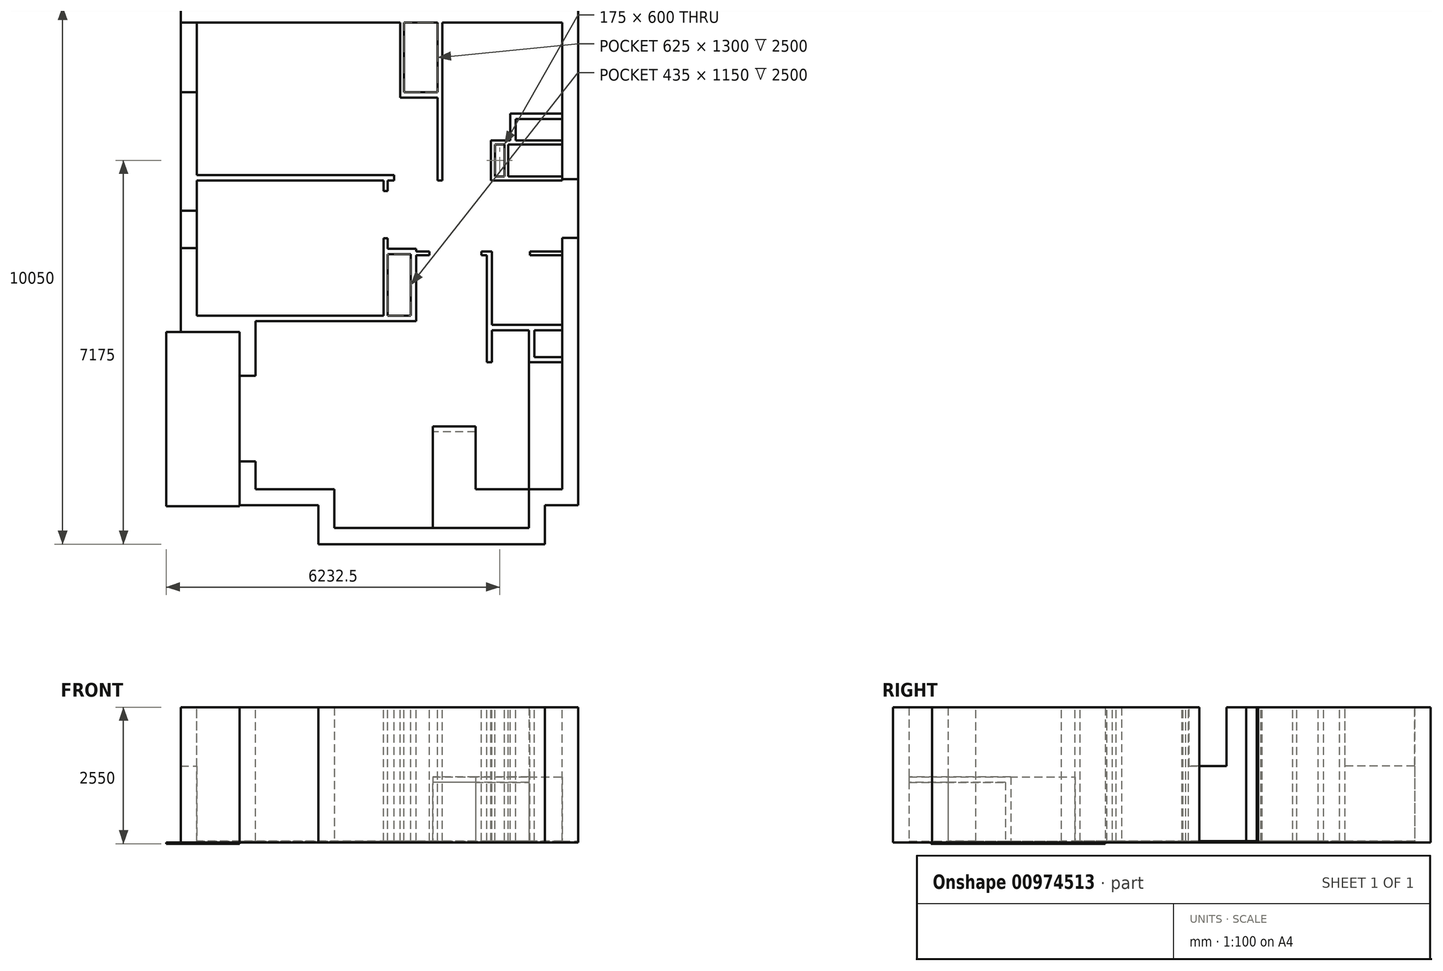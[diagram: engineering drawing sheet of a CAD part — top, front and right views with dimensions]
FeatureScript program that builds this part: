
annotation { "Feature Type Name" : "Feature", "Feature Type Description" : "" }
export const myFeature = defineFeature(function(context is Context, id is Id, definition is map)
    precondition{}
    {
        {
            var Q0;
            Q0=qCreatedBy(makeId("Top.planeOp"),FACE);
            var sketch = newSketch(context, id + "F0", { "sketchPlane" : qUnion([Q0])});
            skLineSegment(sketch, "E0", {"start": v(0, 0) * mm, "end": v(-6830, 0) * mm});
            skLineSegment(sketch, "E1", {"start": v(-6830, 0) * mm, "end": v(-6830, -5480) * mm});
            skLineSegment(sketch, "E2", {"start": v(-6830, -5480) * mm, "end": v(-5730, -5480) * mm});
            skLineSegment(sketch, "E3", {"start": v(-5730, -5480) * mm, "end": v(-5730, -8720) * mm});
            skLineSegment(sketch, "E4", {"start": v(-5730, -8720) * mm, "end": v(-4260, -8720) * mm});
            skLineSegment(sketch, "E5", {"start": v(-4260, -8720) * mm, "end": v(-4260, -9450) * mm});
            skLineSegment(sketch, "E6", {"start": v(-4260, -9450) * mm, "end": v(-620, -9450) * mm});
            skLineSegment(sketch, "E7", {"start": v(-620, -9450) * mm, "end": v(-620, -8720) * mm});
            skLineSegment(sketch, "E8", {"start": v(-620, -8720) * mm, "end": v(0, -8720) * mm});
            skLineSegment(sketch, "E9", {"start": v(0, -8720) * mm, "end": v(0, 0) * mm});
            skLineSegment(sketch, "E10", {"start": v(-7130, 300) * mm, "end": v(300, 300) * mm});
            skLineSegment(sketch, "E11", {"start": v(300, 300) * mm, "end": v(300, -9020) * mm});
            skLineSegment(sketch, "E12", {"start": v(300, -9020) * mm, "end": v(-320, -9020) * mm});
            skLineSegment(sketch, "E13", {"start": v(-320, -9020) * mm, "end": v(-320, -9750) * mm});
            skLineSegment(sketch, "E14", {"start": v(-320, -9750) * mm, "end": v(-4560, -9750) * mm});
            skLineSegment(sketch, "E15", {"start": v(-4560, -9750) * mm, "end": v(-4560, -9020) * mm});
            skLineSegment(sketch, "E16", {"start": v(-4560, -9020) * mm, "end": v(-6030, -9020) * mm});
            skLineSegment(sketch, "E17", {"start": v(-6030, -9020) * mm, "end": v(-6030, -5780) * mm});
            skLineSegment(sketch, "E18", {"start": v(-6030, -5780) * mm, "end": v(-7130, -5780) * mm});
            skLineSegment(sketch, "E19", {"start": v(-7130, -5780) * mm, "end": v(-7130, 300) * mm});
            skSolve(sketch);
        }
        {
            var Q0;
            Q0 = qSketchRegion(id + "F0", true);
            extrude(context, id + "F1", {"entities" : qUnion([Q0]), "depth" : 2500 * mm, "offsetDistance" : 25 * mm});
        }
        {
            var Q0;
            Q0=makeQuery(id+"F1.opExtrude","CAP_FACE",FACE,{"disambiguationData":[OSD([sQuery(id+"F0.wireOp",EDGE,"E0"),sQuery(id+"F0.wireOp",EDGE,"E1"),sQuery(id+"F0.wireOp",EDGE,"E2"),sQuery(id+"F0.wireOp",EDGE,"E3"),sQuery(id+"F0.wireOp",EDGE,"E4"),sQuery(id+"F0.wireOp",EDGE,"E5"),sQuery(id+"F0.wireOp",EDGE,"E6"),sQuery(id+"F0.wireOp",EDGE,"E7"),sQuery(id+"F0.wireOp",EDGE,"E8"),sQuery(id+"F0.wireOp",EDGE,"E9"),sQuery(id+"F0.wireOp",EDGE,"E10"),sQuery(id+"F0.wireOp",EDGE,"E11"),sQuery(id+"F0.wireOp",EDGE,"E12"),sQuery(id+"F0.wireOp",EDGE,"E13"),sQuery(id+"F0.wireOp",EDGE,"E14"),sQuery(id+"F0.wireOp",EDGE,"E15"),sQuery(id+"F0.wireOp",EDGE,"E16"),sQuery(id+"F0.wireOp",EDGE,"E17"),sQuery(id+"F0.wireOp",EDGE,"E18"),sQuery(id+"F0.wireOp",EDGE,"E19")])],"isStart":true});
            var sketch = newSketch(context, id + "F2", { "sketchPlane" : qUnion([Q0])});
            skLineSegment(sketch, "E20.0", {"start": v(-7130, -300) * mm, "end": v(300, -300) * mm});
            skLineSegment(sketch, "E20.1", {"start": v(-7130, 5780) * mm, "end": v(-7130, -300) * mm});
            skLineSegment(sketch, "E20.2", {"start": v(-6030, 5780) * mm, "end": v(-7130, 5780) * mm});
            skLineSegment(sketch, "E20.3", {"start": v(-6030, 9020) * mm, "end": v(-6030, 5780) * mm});
            skLineSegment(sketch, "E20.4", {"start": v(-4560, 9020) * mm, "end": v(-6030, 9020) * mm});
            skLineSegment(sketch, "E20.5", {"start": v(-4560, 9750) * mm, "end": v(-4560, 9020) * mm});
            skLineSegment(sketch, "E20.6", {"start": v(-320, 9750) * mm, "end": v(-4560, 9750) * mm});
            skLineSegment(sketch, "E20.7", {"start": v(-320, 9020) * mm, "end": v(-320, 9750) * mm});
            skLineSegment(sketch, "E20.8", {"start": v(300, 9020) * mm, "end": v(-320, 9020) * mm});
            skLineSegment(sketch, "E20.9", {"start": v(300, -300) * mm, "end": v(300, 9020) * mm});
            skSolve(sketch);
        }
        {
            var Q0;
            Q0 = qSketchRegion(id + "F2", true);
            extrude(context, id + "F3", {"entities" : qUnion([Q0]), "operationType" : NewBodyOperationType.ADD, "depth" : 25 * mm, "offsetDistance" : 25 * mm});
        }
        {
            var Q0;
            Q0=makeQuery(id+"F3.opExtrude","CAP_FACE",FACE,{"disambiguationData":[OSD([sQuery(id+"F2.wireOp",EDGE,"E20.0"),sQuery(id+"F2.wireOp",EDGE,"E20.1"),sQuery(id+"F2.wireOp",EDGE,"E20.2"),sQuery(id+"F2.wireOp",EDGE,"E20.3"),sQuery(id+"F2.wireOp",EDGE,"E20.4"),sQuery(id+"F2.wireOp",EDGE,"E20.5"),sQuery(id+"F2.wireOp",EDGE,"E20.6"),sQuery(id+"F2.wireOp",EDGE,"E20.7"),sQuery(id+"F2.wireOp",EDGE,"E20.8"),sQuery(id+"F2.wireOp",EDGE,"E20.9")])],"isStart":false});
            var sketch = newSketch(context, id + "F4", { "sketchPlane" : qUnion([Q0])});
            skLineSegment(sketch, "E21", {"start": v(-6030, 5780) * mm, "end": v(-7400, 5780) * mm});
            skLineSegment(sketch, "E22", {"start": v(-7400, 5780) * mm, "end": v(-7400, 9040) * mm});
            skLineSegment(sketch, "E23", {"start": v(-7400, 9040) * mm, "end": v(-6030, 9040) * mm});
            skLineSegment(sketch, "E24", {"start": v(-6030, 9040) * mm, "end": v(-6030, 5780) * mm});
            skSolve(sketch);
        }
        {
            var Q0;
            Q0 = qSketchRegion(id + "F4", true);
            extrude(context, id + "F5", {"entities" : qUnion([Q0]), "depth" : 25 * mm, "offsetDistance" : 25 * mm});
        }
        {
            var Q0;
            Q0=makeQuery(id+"F1.opExtrude","CAP_FACE",FACE,{"disambiguationData":[OSD([sQuery(id+"F0.wireOp",EDGE,"E0"),sQuery(id+"F0.wireOp",EDGE,"E1"),sQuery(id+"F0.wireOp",EDGE,"E2"),sQuery(id+"F0.wireOp",EDGE,"E3"),sQuery(id+"F0.wireOp",EDGE,"E4"),sQuery(id+"F0.wireOp",EDGE,"E5"),sQuery(id+"F0.wireOp",EDGE,"E6"),sQuery(id+"F0.wireOp",EDGE,"E7"),sQuery(id+"F0.wireOp",EDGE,"E8"),sQuery(id+"F0.wireOp",EDGE,"E9"),sQuery(id+"F0.wireOp",EDGE,"E10"),sQuery(id+"F0.wireOp",EDGE,"E11"),sQuery(id+"F0.wireOp",EDGE,"E12"),sQuery(id+"F0.wireOp",EDGE,"E13"),sQuery(id+"F0.wireOp",EDGE,"E14"),sQuery(id+"F0.wireOp",EDGE,"E15"),sQuery(id+"F0.wireOp",EDGE,"E16"),sQuery(id+"F0.wireOp",EDGE,"E17"),sQuery(id+"F0.wireOp",EDGE,"E18"),sQuery(id+"F0.wireOp",EDGE,"E19")])],"isStart":false});
            var sketch = newSketch(context, id + "F6", { "sketchPlane" : qUnion([Q0])});
            skLineSegment(sketch, "E25", {"start": v(-6830, -2950) * mm, "end": v(-3340, -2950) * mm});
            skLineSegment(sketch, "E26", {"start": v(-5730, -5480) * mm, "end": v(-3340, -5480) * mm});
            skLineSegment(sketch, "E27", {"start": v(-5730, -5580) * mm, "end": v(-2730, -5580) * mm});
            skLineSegment(sketch, "E28", {"start": v(-2730, -5580) * mm, "end": v(-2730, -4350) * mm});
            skLineSegment(sketch, "E29", {"start": v(-2730, -4230) * mm, "end": v(-3265, -4230) * mm});
            skLineSegment(sketch, "E30", {"start": v(-2830, -5480) * mm, "end": v(-2830, -4330) * mm});
            skLineSegment(sketch, "E31", {"start": v(-2830, -4330) * mm, "end": v(-3265, -4330) * mm});
            skLineSegment(sketch, "E32", {"start": v(-3265, -4330) * mm, "end": v(-3265, -5480) * mm});
            skLineSegment(sketch, "E33", {"start": v(-3340, -4230) * mm, "end": v(-3340, -5480) * mm});
            skLineSegment(sketch, "E34", {"start": v(-2330, 0) * mm, "end": v(-2330, -1300) * mm});
            skLineSegment(sketch, "E35", {"start": v(-2330, -2950) * mm, "end": v(-2240, -2950) * mm});
            skLineSegment(sketch, "E36", {"start": v(-2240, -2950) * mm, "end": v(-2240, 0) * mm});
            skLineSegment(sketch, "E37", {"start": v(-5730, -5580) * mm, "end": v(-5730, -5480) * mm});
            skLineSegment(sketch, "E38", {"start": v(-2240, 0) * mm, "end": v(-2330, 0) * mm});
            skLineSegment(sketch, "E39.trimOffspring", {"start": v(-3265, -5480) * mm, "end": v(-2830, -5480) * mm});
            skLineSegment(sketch, "E40", {"start": v(-3265, -4230) * mm, "end": v(-3265, -4030) * mm});
            skLineSegment(sketch, "E41", {"start": v(-3265, -4030) * mm, "end": v(-3340, -4030) * mm});
            skLineSegment(sketch, "E42", {"start": v(-3340, -4030) * mm, "end": v(-3340, -4230) * mm});
            skLineSegment(sketch, "E43", {"start": v(-2955, 0) * mm, "end": v(-2955, -1300) * mm});
            skLineSegment(sketch, "E44", {"start": v(-2955, -1300) * mm, "end": v(-2330, -1300) * mm});
            skLineSegment(sketch, "E45", {"start": v(-2330, -1400) * mm, "end": v(-3030, -1400) * mm});
            skLineSegment(sketch, "E46", {"start": v(-3030, -1400) * mm, "end": v(-3030, 0) * mm});
            skLineSegment(sketch, "E47", {"start": v(-3030, 0) * mm, "end": v(-2955, 0) * mm});
            skLineSegment(sketch, "E48.trimOffspring", {"start": v(-2330, -1400) * mm, "end": v(-2330, -2950) * mm});
            skLineSegment(sketch, "E49", {"start": v(-3265, -2950) * mm, "end": v(-3265, -3150) * mm});
            skLineSegment(sketch, "E50", {"start": v(-3265, -3150) * mm, "end": v(-3340, -3150) * mm});
            skLineSegment(sketch, "E51", {"start": v(-3340, -3150) * mm, "end": v(-3340, -2950) * mm});
            skLineSegment(sketch, "E52", {"start": v(-3140, -2850) * mm, "end": v(-3140, -2950) * mm});
            skLineSegment(sketch, "E53", {"start": v(-3140, -2950) * mm, "end": v(-3265, -2950) * mm});
            skLineSegment(sketch, "E54", {"start": v(-6830, -2850) * mm, "end": v(-3140, -2850) * mm});
            skLineSegment(sketch, "E55", {"start": v(-6830, -2950) * mm, "end": v(-6830, -2850) * mm});
            skLineSegment(sketch, "E56", {"start": v(-2730, -4275) * mm, "end": v(-2480, -4275) * mm});
            skLineSegment(sketch, "E57", {"start": v(-2480, -4275) * mm, "end": v(-2480, -4350) * mm});
            skLineSegment(sketch, "E58", {"start": v(-2480, -4350) * mm, "end": v(-2730, -4350) * mm});
            skLineSegment(sketch, "E59.trimOffspring", {"start": v(-2730, -4275) * mm, "end": v(-2730, -4230) * mm});
            skSolve(sketch);
        }
        {
            var Q0;
            Q0 = qSketchRegion(id + "F6", true);
            extrude(context, id + "F7", {"entities" : qUnion([Q0]), "operationType" : NewBodyOperationType.ADD, "endBound" : BoundingType.UP_TO_NEXT, "oppositeDirection" : true, "depth" : 25 * mm, "offsetDistance" : 25 * mm});
        }
        {
            var Q0;
            Q0=makeQuery(id+"F7.boolean.opBoolean","MERGE",FACE,{"derivedFrom":[makeQuery(id+"F1.opExtrude","CAP_FACE",FACE,{"disambiguationData":[OSD([sQuery(id+"F0.wireOp",EDGE,"E0"),sQuery(id+"F0.wireOp",EDGE,"E1"),sQuery(id+"F0.wireOp",EDGE,"E2"),sQuery(id+"F0.wireOp",EDGE,"E3"),sQuery(id+"F0.wireOp",EDGE,"E4"),sQuery(id+"F0.wireOp",EDGE,"E5"),sQuery(id+"F0.wireOp",EDGE,"E6"),sQuery(id+"F0.wireOp",EDGE,"E7"),sQuery(id+"F0.wireOp",EDGE,"E8"),sQuery(id+"F0.wireOp",EDGE,"E9"),sQuery(id+"F0.wireOp",EDGE,"E10"),sQuery(id+"F0.wireOp",EDGE,"E11"),sQuery(id+"F0.wireOp",EDGE,"E12"),sQuery(id+"F0.wireOp",EDGE,"E13"),sQuery(id+"F0.wireOp",EDGE,"E14"),sQuery(id+"F0.wireOp",EDGE,"E15"),sQuery(id+"F0.wireOp",EDGE,"E16"),sQuery(id+"F0.wireOp",EDGE,"E17"),sQuery(id+"F0.wireOp",EDGE,"E18"),sQuery(id+"F0.wireOp",EDGE,"E19")])],"isStart":false}),makeQuery(id+"F7.opExtrude","CAP_FACE",FACE,{"disambiguationData":[OSD([sQuery(id+"F6.wireOp",EDGE,"E25"),sQuery(id+"F6.wireOp",EDGE,"E49"),sQuery(id+"F6.wireOp",EDGE,"E50"),sQuery(id+"F6.wireOp",EDGE,"E51"),sQuery(id+"F6.wireOp",EDGE,"E52"),sQuery(id+"F6.wireOp",EDGE,"E53"),sQuery(id+"F6.wireOp",EDGE,"E54"),sQuery(id+"F6.wireOp",EDGE,"E55")])],"isStart":true}),makeQuery(id+"F7.opExtrude","CAP_FACE",FACE,{"disambiguationData":[OSD([sQuery(id+"F6.wireOp",EDGE,"E26"),sQuery(id+"F6.wireOp",EDGE,"E27"),sQuery(id+"F6.wireOp",EDGE,"E28"),sQuery(id+"F6.wireOp",EDGE,"E29"),sQuery(id+"F6.wireOp",EDGE,"E30"),sQuery(id+"F6.wireOp",EDGE,"E31"),sQuery(id+"F6.wireOp",EDGE,"E32"),sQuery(id+"F6.wireOp",EDGE,"E33"),sQuery(id+"F6.wireOp",EDGE,"E37"),sQuery(id+"F6.wireOp",EDGE,"E39.trimOffspring"),sQuery(id+"F6.wireOp",EDGE,"E40"),sQuery(id+"F6.wireOp",EDGE,"E41"),sQuery(id+"F6.wireOp",EDGE,"E42")])],"isStart":true}),makeQuery(id+"F7.opExtrude","CAP_FACE",FACE,{"disambiguationData":[OSD([sQuery(id+"F6.wireOp",EDGE,"E34"),sQuery(id+"F6.wireOp",EDGE,"E35"),sQuery(id+"F6.wireOp",EDGE,"E36"),sQuery(id+"F6.wireOp",EDGE,"E38"),sQuery(id+"F6.wireOp",EDGE,"E43"),sQuery(id+"F6.wireOp",EDGE,"E44"),sQuery(id+"F6.wireOp",EDGE,"E45"),sQuery(id+"F6.wireOp",EDGE,"E46"),sQuery(id+"F6.wireOp",EDGE,"E47"),sQuery(id+"F6.wireOp",EDGE,"E48.trimOffspring")])],"isStart":true})]});
            var sketch = newSketch(context, id + "F8", { "sketchPlane" : qUnion([Q0])});
            skLineSegment(sketch, "E60", {"start": v(0, -6350) * mm, "end": v(-620, -6350) * mm});
            skLineSegment(sketch, "E61", {"start": v(-620, -6350) * mm, "end": v(-620, -5750) * mm});
            skLineSegment(sketch, "E62", {"start": v(0, -5650) * mm, "end": v(0, -5750) * mm});
            skLineSegment(sketch, "E63", {"start": v(0, -5750) * mm, "end": v(-520, -5750) * mm});
            skLineSegment(sketch, "E64", {"start": v(-520, -5750) * mm, "end": v(-520, -6250) * mm});
            skLineSegment(sketch, "E65", {"start": v(-520, -6250) * mm, "end": v(0, -6250) * mm});
            skLineSegment(sketch, "E66", {"start": v(0, -6350) * mm, "end": v(0, -6250) * mm});
            skLineSegment(sketch, "E67", {"start": v(-620, -5750) * mm, "end": v(-1310, -5750) * mm});
            skLineSegment(sketch, "E68", {"start": v(-1310, -5750) * mm, "end": v(-1310, -6350) * mm});
            skLineSegment(sketch, "E69", {"start": v(-1310, -6350) * mm, "end": v(-1410, -6350) * mm});
            skLineSegment(sketch, "E70", {"start": v(-1410, -6350) * mm, "end": v(-1410, -4350) * mm});
            skLineSegment(sketch, "E71", {"start": v(-1410, -4350) * mm, "end": v(-1510, -4350) * mm});
            skLineSegment(sketch, "E72", {"start": v(-1510, -4350) * mm, "end": v(-1510, -4275) * mm});
            skLineSegment(sketch, "E73", {"start": v(-1510, -4275) * mm, "end": v(-1310, -4275) * mm});
            skLineSegment(sketch, "E74", {"start": v(-1310, -4275) * mm, "end": v(-1310, -5650) * mm});
            skLineSegment(sketch, "E75", {"start": v(-1310, -5650) * mm, "end": v(0, -5650) * mm});
            skLineSegment(sketch, "E76", {"start": v(0, -4350) * mm, "end": v(-600, -4350) * mm});
            skLineSegment(sketch, "E77", {"start": v(-600, -4350) * mm, "end": v(-600, -4275) * mm});
            skLineSegment(sketch, "E78", {"start": v(-600, -4275) * mm, "end": v(0, -4275) * mm});
            skLineSegment(sketch, "E79", {"start": v(0, -4275) * mm, "end": v(0, -4350) * mm});
            skLineSegment(sketch, "E80", {"start": v(0, -2275) * mm, "end": v(0, -2200) * mm});
            skLineSegment(sketch, "E81", {"start": v(0, -2200) * mm, "end": v(-870, -2200) * mm});
            skLineSegment(sketch, "E82", {"start": v(-870, -2200) * mm, "end": v(-870, -1800) * mm});
            skLineSegment(sketch, "E83", {"start": v(-870, -1800) * mm, "end": v(0, -1800) * mm});
            skLineSegment(sketch, "E84", {"start": v(0, -1800) * mm, "end": v(0, -1700) * mm});
            skLineSegment(sketch, "E85", {"start": v(0, -1700) * mm, "end": v(-970, -1700) * mm});
            skLineSegment(sketch, "E86", {"start": v(-970, -1700) * mm, "end": v(-970, -2200) * mm});
            skLineSegment(sketch, "E87", {"start": v(-970, -2200) * mm, "end": v(-1330, -2200) * mm});
            skLineSegment(sketch, "E88", {"start": v(-1080, -2275) * mm, "end": v(-1080, -2875) * mm});
            skLineSegment(sketch, "E89", {"start": v(-1330, -2950) * mm, "end": v(0, -2950) * mm});
            skLineSegment(sketch, "E90", {"start": v(0, -2950) * mm, "end": v(0, -2875) * mm});
            skLineSegment(sketch, "E91", {"start": v(0, -2275) * mm, "end": v(-1005, -2275) * mm});
            skLineSegment(sketch, "E92", {"start": v(-1005, -2275) * mm, "end": v(-1005, -2875) * mm});
            skLineSegment(sketch, "E93", {"start": v(-1005, -2875) * mm, "end": v(0, -2875) * mm});
            skLineSegment(sketch, "E94", {"start": v(-1080, -2875) * mm, "end": v(-1255, -2875) * mm});
            skLineSegment(sketch, "E95", {"start": v(-1255, -2875) * mm, "end": v(-1255, -2275) * mm});
            skLineSegment(sketch, "E96", {"start": v(-1255, -2275) * mm, "end": v(-1080, -2275) * mm});
            skLineSegment(sketch, "E97", {"start": v(-1330, -2200) * mm, "end": v(-1330, -2950) * mm});
            skSolve(sketch);
        }
        {
            var Q0;
            Q0 = qSketchRegion(id + "F8", true);
            extrude(context, id + "F9", {"entities" : qUnion([Q0]), "endBound" : BoundingType.UP_TO_NEXT, "oppositeDirection" : true, "depth" : 25 * mm, "offsetDistance" : 25 * mm});
        }
        {
            var Q0;
            Q0=makeQuery(id+"F7.boolean.opBoolean","MERGE",FACE,{"derivedFrom":[makeQuery(id+"F1.opExtrude","CAP_FACE",FACE,{"disambiguationData":[OSD([sQuery(id+"F0.wireOp",EDGE,"E0"),sQuery(id+"F0.wireOp",EDGE,"E1"),sQuery(id+"F0.wireOp",EDGE,"E2"),sQuery(id+"F0.wireOp",EDGE,"E3"),sQuery(id+"F0.wireOp",EDGE,"E4"),sQuery(id+"F0.wireOp",EDGE,"E5"),sQuery(id+"F0.wireOp",EDGE,"E6"),sQuery(id+"F0.wireOp",EDGE,"E7"),sQuery(id+"F0.wireOp",EDGE,"E8"),sQuery(id+"F0.wireOp",EDGE,"E9"),sQuery(id+"F0.wireOp",EDGE,"E10"),sQuery(id+"F0.wireOp",EDGE,"E11"),sQuery(id+"F0.wireOp",EDGE,"E12"),sQuery(id+"F0.wireOp",EDGE,"E13"),sQuery(id+"F0.wireOp",EDGE,"E14"),sQuery(id+"F0.wireOp",EDGE,"E15"),sQuery(id+"F0.wireOp",EDGE,"E16"),sQuery(id+"F0.wireOp",EDGE,"E17"),sQuery(id+"F0.wireOp",EDGE,"E18"),sQuery(id+"F0.wireOp",EDGE,"E19")])],"isStart":false}),makeQuery(id+"F7.opExtrude","CAP_FACE",FACE,{"disambiguationData":[OSD([sQuery(id+"F6.wireOp",EDGE,"E25"),sQuery(id+"F6.wireOp",EDGE,"E49"),sQuery(id+"F6.wireOp",EDGE,"E50"),sQuery(id+"F6.wireOp",EDGE,"E51"),sQuery(id+"F6.wireOp",EDGE,"E52"),sQuery(id+"F6.wireOp",EDGE,"E53"),sQuery(id+"F6.wireOp",EDGE,"E54"),sQuery(id+"F6.wireOp",EDGE,"E55")])],"isStart":true}),makeQuery(id+"F7.opExtrude","CAP_FACE",FACE,{"disambiguationData":[OSD([sQuery(id+"F6.wireOp",EDGE,"E26"),sQuery(id+"F6.wireOp",EDGE,"E27"),sQuery(id+"F6.wireOp",EDGE,"E28"),sQuery(id+"F6.wireOp",EDGE,"E29"),sQuery(id+"F6.wireOp",EDGE,"E30"),sQuery(id+"F6.wireOp",EDGE,"E31"),sQuery(id+"F6.wireOp",EDGE,"E32"),sQuery(id+"F6.wireOp",EDGE,"E33"),sQuery(id+"F6.wireOp",EDGE,"E37"),sQuery(id+"F6.wireOp",EDGE,"E39.trimOffspring"),sQuery(id+"F6.wireOp",EDGE,"E40"),sQuery(id+"F6.wireOp",EDGE,"E41"),sQuery(id+"F6.wireOp",EDGE,"E42"),sQuery(id+"F6.wireOp",EDGE,"E56"),sQuery(id+"F6.wireOp",EDGE,"E57"),sQuery(id+"F6.wireOp",EDGE,"E58"),sQuery(id+"F6.wireOp",EDGE,"E59.trimOffspring")])],"isStart":true}),makeQuery(id+"F7.opExtrude","CAP_FACE",FACE,{"disambiguationData":[OSD([sQuery(id+"F6.wireOp",EDGE,"E34"),sQuery(id+"F6.wireOp",EDGE,"E35"),sQuery(id+"F6.wireOp",EDGE,"E36"),sQuery(id+"F6.wireOp",EDGE,"E38"),sQuery(id+"F6.wireOp",EDGE,"E43"),sQuery(id+"F6.wireOp",EDGE,"E44"),sQuery(id+"F6.wireOp",EDGE,"E45"),sQuery(id+"F6.wireOp",EDGE,"E46"),sQuery(id+"F6.wireOp",EDGE,"E47"),sQuery(id+"F6.wireOp",EDGE,"E48.trimOffspring")])],"isStart":true})]});
            var sketch = newSketch(context, id + "F10", { "sketchPlane" : qUnion([Q0])});
            skLineSegment(sketch, "E98", {"start": v(300, -2925) * mm, "end": v(0, -2925) * mm});
            skLineSegment(sketch, "E99", {"start": v(0, -2925) * mm, "end": v(0, -4025) * mm});
            skLineSegment(sketch, "E100", {"start": v(0, -4025) * mm, "end": v(300, -4025) * mm});
            skLineSegment(sketch, "E101", {"start": v(300, -4025) * mm, "end": v(300, -2925) * mm});
            skLineSegment(sketch, "E102", {"start": v(-5730, -8200) * mm, "end": v(-6030, -8200) * mm});
            skLineSegment(sketch, "E103", {"start": v(-6030, -8200) * mm, "end": v(-6030, -6600) * mm});
            skLineSegment(sketch, "E104", {"start": v(-6030, -6600) * mm, "end": v(-5730, -6600) * mm});
            skLineSegment(sketch, "E105", {"start": v(-5730, -6600) * mm, "end": v(-5730, -8200) * mm});
            skLineSegment(sketch, "E106", {"start": v(-6830, -4215) * mm, "end": v(-7130, -4215) * mm});
            skLineSegment(sketch, "E107", {"start": v(-7130, -4215) * mm, "end": v(-7130, -3515) * mm});
            skLineSegment(sketch, "E108", {"start": v(-7130, -3515) * mm, "end": v(-6830, -3515) * mm});
            skLineSegment(sketch, "E109", {"start": v(-6830, -3515) * mm, "end": v(-6830, -4215) * mm});
            skLineSegment(sketch, "E110", {"start": v(-6830, -1300) * mm, "end": v(-7130, -1300) * mm});
            skLineSegment(sketch, "E111", {"start": v(-7130, -1300) * mm, "end": v(-7130, 0) * mm});
            skLineSegment(sketch, "E112", {"start": v(-7130, 0) * mm, "end": v(-6830, 0) * mm});
            skLineSegment(sketch, "E113", {"start": v(-6830, 0) * mm, "end": v(-6830, -1300) * mm});
            skSolve(sketch);
        }
        {
            var Q0;
            Q0=makeQuery(id+"F10.imprint","IMPRINT",FACE,{"disambiguationData":[TD([[makeQuery(id+"F10.imprint","IMPRINT",EDGE,{"derivedFrom":sQuery(id+"F10.wireOp",EDGE,"E102")}),-1.0]])]});
            var Q1;
            Q1=makeQuery(id+"F10.imprint","IMPRINT",FACE,{"disambiguationData":[TD([[makeQuery(id+"F10.imprint","IMPRINT",EDGE,{"derivedFrom":sQuery(id+"F10.wireOp",EDGE,"E98")}),1.0]])]});
            var Q2;
            Q2=sQuery(id+"F10.wireOp",EDGE,"E104");
            var Q3;
            Q3=sQuery(id+"F10.wireOp",EDGE,"E103");
            var Q4;
            Q4=sQuery(id+"F10.wireOp",EDGE,"E105");
            var Q5;
            Q5=sQuery(id+"F10.wireOp",EDGE,"E102");
            var Q6;
            Q6=sQuery(id+"F10.wireOp",EDGE,"E101");
            var Q7;
            Q7=sQuery(id+"F10.wireOp",EDGE,"E100");
            var Q8;
            Q8=sQuery(id+"F10.wireOp",EDGE,"E99");
            var Q9;
            Q9=sQuery(id+"F10.wireOp",EDGE,"E98");
            extrude(context, id + "F11", {"entities" : qUnion([Q0, Q1]), "operationType" : NewBodyOperationType.REMOVE, "surfaceEntities" : qUnion([Q2, Q3, Q4, Q5, Q6, Q7, Q8, Q9]), "oppositeDirection" : true, "depth" : 2500 * mm, "offsetDistance" : 25 * mm});
        }
        {
            var Q0;
            Q0 = qSketchRegion(id + "F10", true);
            extrude(context, id + "F12", {"entities" : qUnion([Q0]), "operationType" : NewBodyOperationType.REMOVE, "oppositeDirection" : true, "depth" : 1100 * mm, "offsetDistance" : 25 * mm});
        }
        {
            var Q0;
            Q0=makeQuery(id+"F11.boolean.opBoolean","MERGE",FACE,{"derivedFrom":[makeQuery(id+"F7.boolean.opBoolean","SPLIT",FACE,{"disambiguationData":[TD([makeQuery(id+"F1.opExtrude","SWEPT_FACE",FACE,{"disambiguationData":[OSD([sQuery(id+"F0.wireOp",EDGE,"E1")])]})])],"derivedFrom":makeQuery(id+"F3.opExtrude","CAP_FACE",FACE,{"disambiguationData":[OSD([sQuery(id+"F2.wireOp",EDGE,"E20.0"),sQuery(id+"F2.wireOp",EDGE,"E20.1"),sQuery(id+"F2.wireOp",EDGE,"E20.2"),sQuery(id+"F2.wireOp",EDGE,"E20.3"),sQuery(id+"F2.wireOp",EDGE,"E20.4"),sQuery(id+"F2.wireOp",EDGE,"E20.5"),sQuery(id+"F2.wireOp",EDGE,"E20.6"),sQuery(id+"F2.wireOp",EDGE,"E20.7"),sQuery(id+"F2.wireOp",EDGE,"E20.8"),sQuery(id+"F2.wireOp",EDGE,"E20.9")])],"isStart":true})})],"fromTools":[makeQuery(id+"F11.opExtrude","CAP_FACE",FACE,{"disambiguationData":[OSD([sQuery(id+"F10.wireOp",EDGE,"E98"),sQuery(id+"F10.wireOp",EDGE,"E99"),sQuery(id+"F10.wireOp",EDGE,"E100"),sQuery(id+"F10.wireOp",EDGE,"E101")])],"isStart":false}),makeQuery(id+"F11.opExtrude","CAP_FACE",FACE,{"disambiguationData":[OSD([sQuery(id+"F10.wireOp",EDGE,"E102"),sQuery(id+"F10.wireOp",EDGE,"E103"),sQuery(id+"F10.wireOp",EDGE,"E104"),sQuery(id+"F10.wireOp",EDGE,"E105")])],"isStart":false})]});
            var sketch = newSketch(context, id + "F13", { "sketchPlane" : qUnion([Q0])});
            skLineSegment(sketch, "E114", {"start": v(-620, -8720) * mm, "end": v(-620, -6350) * mm});
            skLineSegment(sketch, "E115", {"start": v(-620, -6350) * mm, "end": v(0, -6350) * mm});
            skLineSegment(sketch, "E116", {"start": v(0, -6350) * mm, "end": v(0, -8720) * mm});
            skLineSegment(sketch, "E117", {"start": v(0, -8720) * mm, "end": v(-620, -8720) * mm});
            skLineSegment(sketch, "E118", {"start": v(-620, -8720) * mm, "end": v(-1620, -8720) * mm});
            skLineSegment(sketch, "E119", {"start": v(-1620, -8720) * mm, "end": v(-1620, -7550) * mm});
            skLineSegment(sketch, "E120", {"start": v(-1620, -7550) * mm, "end": v(-2420, -7550) * mm});
            skLineSegment(sketch, "E121", {"start": v(-2420, -7550) * mm, "end": v(-2420, -9450) * mm});
            skLineSegment(sketch, "E122", {"start": v(-2420, -9450) * mm, "end": v(-620, -9450) * mm});
            skLineSegment(sketch, "E123", {"start": v(-620, -9450) * mm, "end": v(-620, -8720) * mm});
            skSolve(sketch);
        }
        {
            var Q0;
            Q0 = qSketchRegion(id + "F13", true);
            extrude(context, id + "F14", {"entities" : qUnion([Q0]), "depth" : 1200 * mm, "offsetDistance" : 25 * mm});
        }
        {
            var Q0;
            Q0=makeQuery(id+"F14.opExtrude","SWEPT_FACE",FACE,{"disambiguationData":[OSD([sQuery(id+"F13.wireOp",EDGE,"E121")])]});
            var sketch = newSketch(context, id + "F15", { "sketchPlane" : qUnion([Q0])});
            skLineSegment(sketch, "E124", {"start": v(9450, 1100) * mm, "end": v(9450, 0) * mm});
            skLineSegment(sketch, "E125", {"start": v(9450, 0) * mm, "end": v(7650, 0) * mm});
            skLineSegment(sketch, "E126", {"start": v(7650, 0) * mm, "end": v(7650, 1100) * mm});
            skLineSegment(sketch, "E127", {"start": v(9450, 1100) * mm, "end": v(7650, 1100) * mm});
            skSolve(sketch);
        }
        {
            var Q0;
            Q0 = qSketchRegion(id + "F15", true);
            extrude(context, id + "F16", {"entities" : qUnion([Q0]), "operationType" : NewBodyOperationType.REMOVE, "endBound" : BoundingType.UP_TO_NEXT, "oppositeDirection" : true, "depth" : 25 * mm, "offsetDistance" : 25 * mm});
        }
    });
